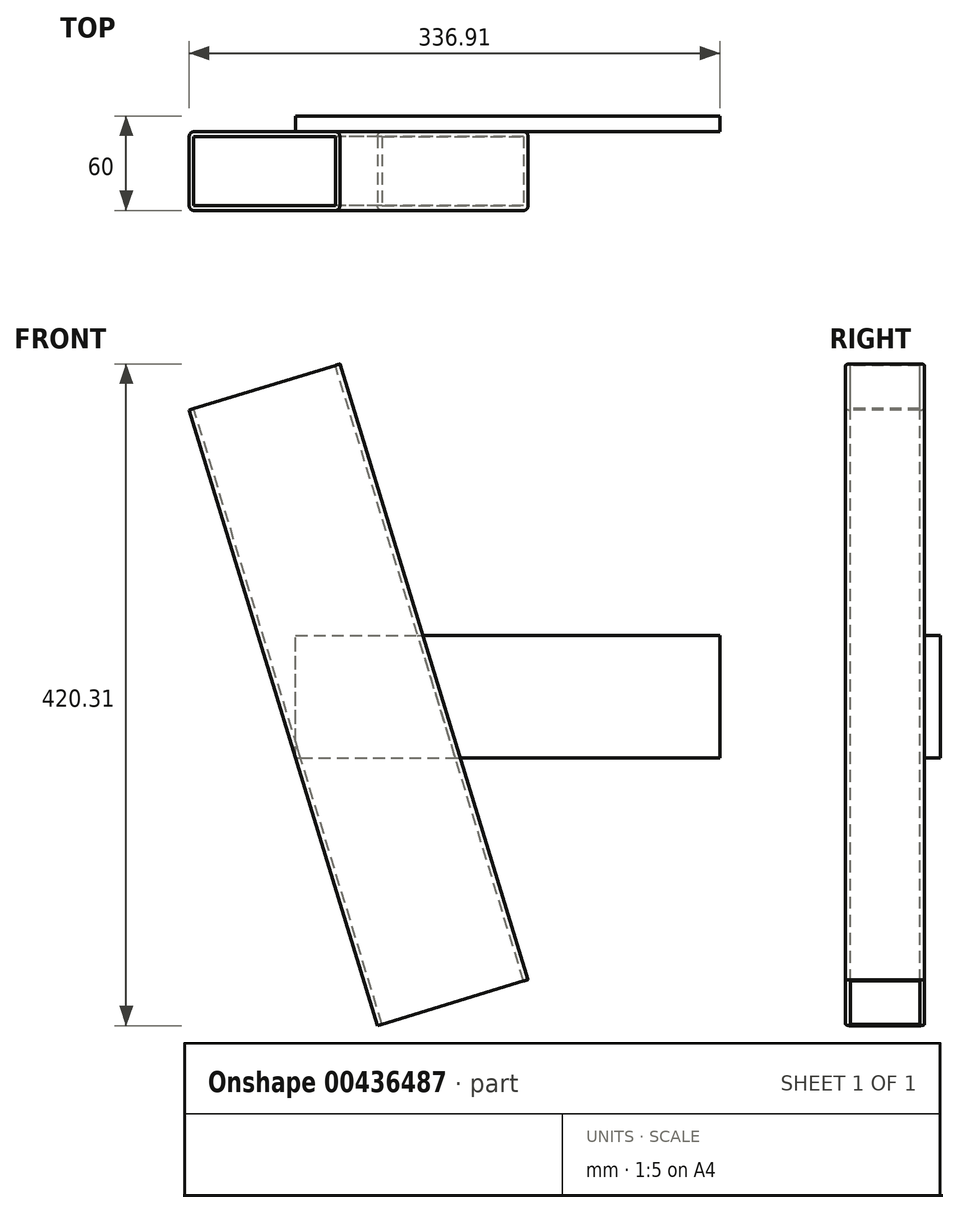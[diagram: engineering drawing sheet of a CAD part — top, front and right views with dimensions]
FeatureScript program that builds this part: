
annotation { "Feature Type Name" : "Feature", "Feature Type Description" : "" }
export const myFeature = defineFeature(function(context is Context, id is Id, definition is map)
    precondition{}
    {
        {
            var Q0;
            Q0=qCreatedBy(makeId("Front.planeOp"),FACE);
            var sketch = newSketch(context, id + "F0", { "sketchPlane" : qUnion([Q0])});
            skLineSegment(sketch, "E0", {"start": v(0, 66.57) * mm, "end": v(0, 0) * mm, "construction": true});
            skLineSegment(sketch, "E1", {"start": v(0, 0) * mm, "end": v(-84.6, -25.87) * mm, "construction": true});
            skSolve(sketch);
        }
        {
            var Q0;
            Q0=qCreatedBy(makeId("Top.planeOp"),FACE);
            var Q1;
            Q1=sQuery(id+"F0.wireOp",EDGE,"E1");
            cPlane(context, id + "F1", {"entities" : qUnion([Q0, Q1]), "cplaneType" : CPlaneType.LINE_ANGLE, "offset" : 25.4 * mm, "angle" : 0 * degree, "width" : 152.4 * mm, "height" : 152.4 * mm});
        }
        {
            var Q0;
            Q0=qCreatedBy(id+"F1.planeOp",FACE);
            var sketch = newSketch(context, id + "F2", { "sketchPlane" : qUnion([Q0])});
            skLineSegment(sketch, "E2.bottom", {"start": v(-47, -25) * mm, "end": v(47, -25) * mm});
            skLineSegment(sketch, "E2.top", {"start": v(-47, 25) * mm, "end": v(47, 25) * mm});
            skLineSegment(sketch, "E2.left", {"start": v(-50, -22) * mm, "end": v(-50, 22) * mm});
            skLineSegment(sketch, "E2.right", {"start": v(50, -22) * mm, "end": v(50, 22) * mm});
            skLineSegment(sketch, "E3", {"start": v(50, -25) * mm, "end": v(-50, 25) * mm, "construction": true});
            skLineSegment(sketch, "E4.0", {"start": v(-47, -22) * mm, "end": v(47, -22) * mm});
            skLineSegment(sketch, "E4.1", {"start": v(-47, -22) * mm, "end": v(-47, 22) * mm});
            skLineSegment(sketch, "E4.2", {"start": v(-47, 22) * mm, "end": v(47, 22) * mm});
            skLineSegment(sketch, "E4.3", {"start": v(47, -22) * mm, "end": v(47, 22) * mm});
            skPoint(sketch, "E5.visualSharp", {"position": v(-50, -25) * mm});
            skArc(sketch, "E5.filletArc", {"start": v(-50, -22) * mm, "mid": v(-49.12, -24.12) * mm, "end": v(-47, -25) * mm});
            skPoint(sketch, "E6.visualSharp", {"position": v(50, -25) * mm});
            skArc(sketch, "E6.filletArc", {"start": v(47, -25) * mm, "mid": v(49.12, -24.12) * mm, "end": v(50, -22) * mm});
            skPoint(sketch, "E7.visualSharp", {"position": v(50, 25) * mm});
            skArc(sketch, "E7.filletArc", {"start": v(50, 22) * mm, "mid": v(49.12, 24.12) * mm, "end": v(47, 25) * mm});
            skPoint(sketch, "E8.visualSharp", {"position": v(-50, 25) * mm});
            skArc(sketch, "E8.filletArc", {"start": v(-47, 25) * mm, "mid": v(-49.12, 24.12) * mm, "end": v(-50, 22) * mm});
            skSolve(sketch);
        }
        {
            var Q0;
            Q0=makeQuery(id+"F2.imprint","IMPRINT",FACE,{"disambiguationData":[TD([[makeQuery(id+"F2.imprint","IMPRINT",EDGE,{"derivedFrom":sQuery(id+"F2.wireOp",EDGE,"E2.bottom")}),1.0]])]});
            extrude(context, id + "F3", {"entities" : qUnion([Q0]), "depth" : 203.2 * mm, "hasSecondDirection" : true, "secondDirectionOppositeDirection" : true, "secondDirectionDepth" : 205.74 * mm});
        }
        {
            var Q0;
            Q0=makeQuery(id+"F3.opExtrude","SWEPT_FACE",FACE,{"disambiguationData":[OSD([sQuery(id+"F2.wireOp",EDGE,"E2.bottom")])]});
            var sketch = newSketch(context, id + "F4", { "sketchPlane" : qUnion([Q0])});
            skLineSegment(sketch, "E9.bottom", {"start": v(40.36, -39) * mm, "end": v(-228.94, -39) * mm});
            skLineSegment(sketch, "E9.top", {"start": v(40.36, 39) * mm, "end": v(-228.94, 39) * mm});
            skLineSegment(sketch, "E9.left", {"start": v(40.36, -39) * mm, "end": v(40.36, 39) * mm});
            skLineSegment(sketch, "E9.right", {"start": v(-228.94, -39) * mm, "end": v(-228.94, 39) * mm});
            skPoint(sketch, "E10", {"position": v(-38.06, 39) * mm});
            skLineSegment(sketch, "E11", {"start": v(40.36, 0) * mm, "end": v(-228.94, 0) * mm, "construction": true});
            skSolve(sketch);
        }
        {
            var Q0;
            Q0 = qSketchRegion(id + "F4", true);
            extrude(context, id + "F5", {"entities" : qUnion([Q0]), "operationType" : NewBodyOperationType.ADD, "depth" : 10 * mm});
        }
    });
